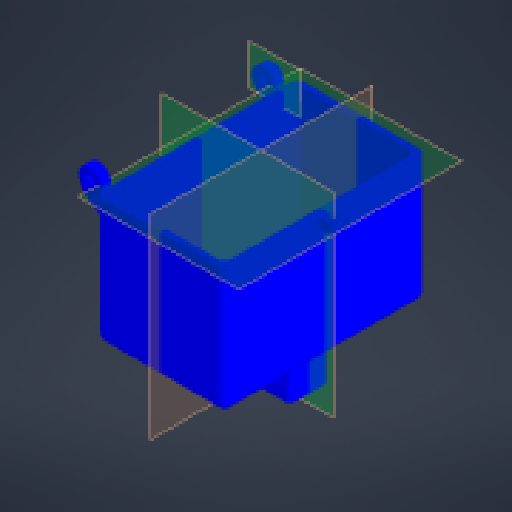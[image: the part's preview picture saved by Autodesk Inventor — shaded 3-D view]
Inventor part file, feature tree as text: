
AUTODESK INVENTOR PART (.ipt)
format: ipt  version: 2024 (Build 280153000, 153)  size: 438,272 bytes
history: native  units: mm
features: other x14, sketch x8, extrude x8, fillet x5, reference x5, mirror x2, projected_geometry x2
ambient origin geometry x8: Origin, YZ Plane, XZ Plane, XY Plane, X Axis, Y Axis, Z Axis, Center Point
bodies: Body1 (feature_tree)
feature tree (44):
  other  "Твердое тело1"
  sketch  "Эскиз1"
  other  "РабПлоскость1"
  extrude  "Выдавливание1"  Depth=15.0mm
  extrude  "Выдавливание2"  Depth=15.0mm
  extrude  "Выдавливание3"  Depth=3.0mm
  extrude  "Выдавливание4"  Depth=10.0mm TaperAngle=0.0deg
  fillet  "Сопряжение3"  Radius=3.0mm
  fillet  "Сопряжение5"  Radius=3.0mm
  fillet  "Сопряжение6"  Radius=3.0mm
  fillet  "Сопряжение8"  Radius=17.0mm
  fillet  "Сопряжение9"  Radius=3.0mm
  extrude  "Выдавливание13"  Depth=3.0mm
  other  "РабПлоскость11"
  extrude  "Выдавливание16"  Depth=3.0mm
  other  "РабПлоскость12"
  mirror  "Зеркальное отражение6"
  other  "РабПлоскость13"
  extrude  "Выдавливание17"  Depth=63.25mm TaperAngle=0.0deg
  other  "РабПлоскость14"
  mirror  "Зеркальное отражение7"
  extrude  "Выдавливание18"  Depth=4.0mm
  reference  "Ссылка1"
  reference  "Ссылка2"
  reference  "Ссылка3"
  reference  "Ссылка4"
  sketch  "Эскиз2"
  sketch  "Эскиз3"
  sketch  "Эскиз4"
  reference  "Ссылка21"
  projected_geometry  "Спроецированная петля1"
  projected_geometry  "Спроецированная петля2"
  sketch  "Эскиз19"
  sketch  "Эскиз24"
  sketch  "Эскиз26"
  sketch  "Эскиз27"
  parser-record x2  (decoder bookkeeping rows leaked as tree rows — omitted from the tree; the rows remain in map.json)
  other  "main_assembly.iam"
  other  "base_assembly:1"
  other  "section:4"
  other  "main axis:1"
  other  "back_box_asembly.iam"
  other  "back_box_cup:1"
note: 2 file-system paths scrubbed to <path> (originals preserved in map.json)
